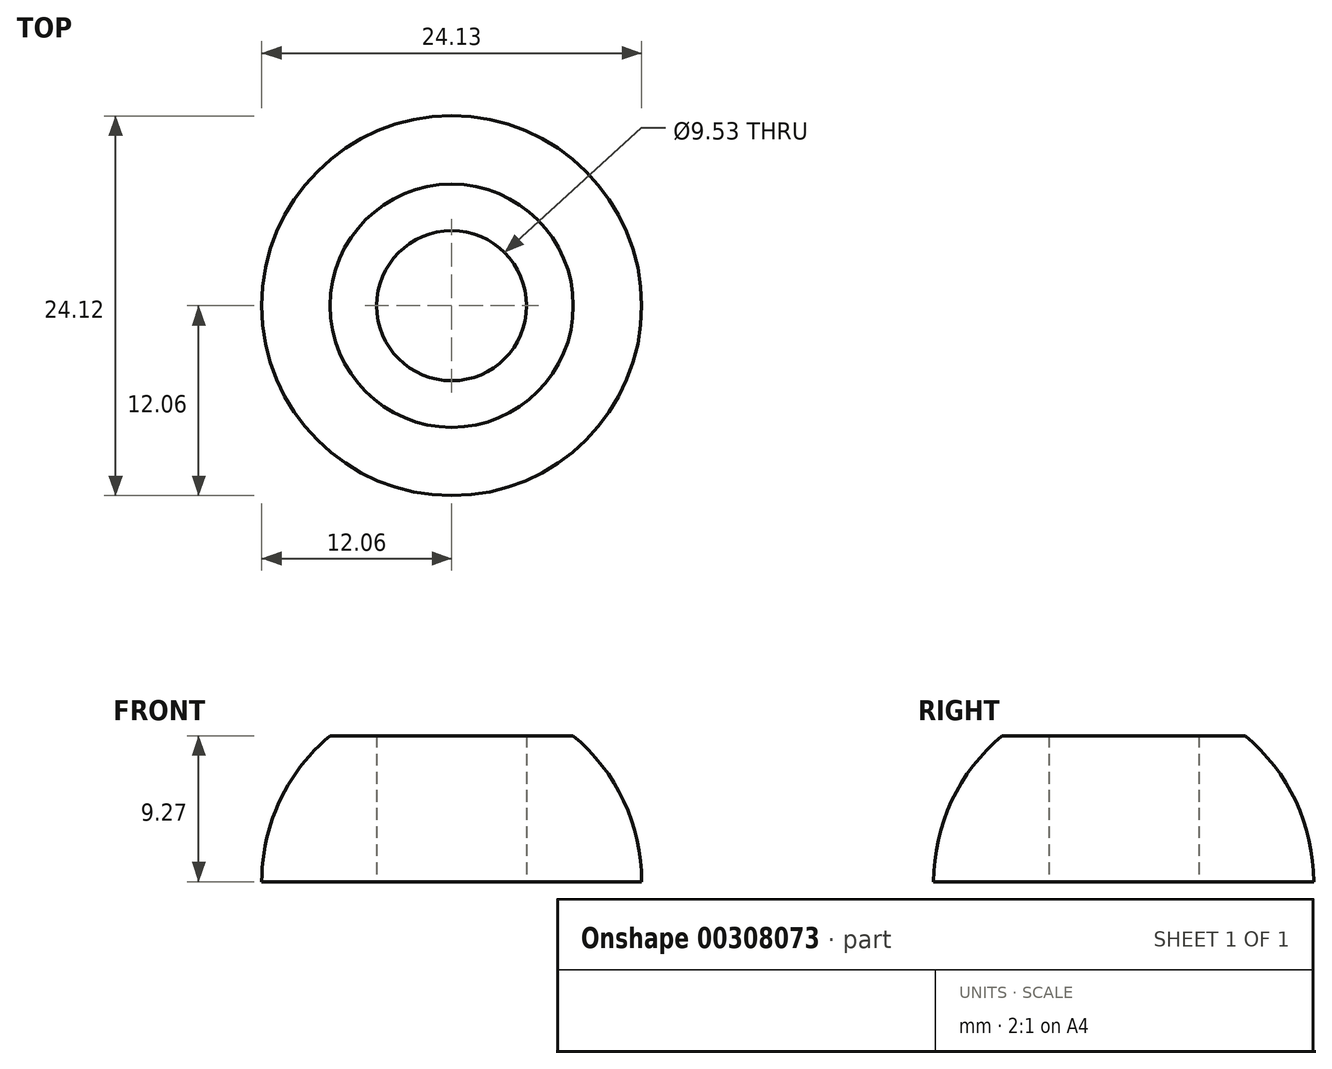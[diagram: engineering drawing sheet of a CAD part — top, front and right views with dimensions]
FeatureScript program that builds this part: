
annotation { "Feature Type Name" : "Feature", "Feature Type Description" : "" }
export const myFeature = defineFeature(function(context is Context, id is Id, definition is map)
    precondition{}
    {
        {
            var Q0;
            Q0=qCreatedBy(makeId("Front.planeOp"),FACE);
            var sketch = newSketch(context, id + "F0", { "sketchPlane" : qUnion([Q0])});
            skArc(sketch, "E0", {"start": v(12.07, 0) * mm, "mid": v(10.93, 5.12) * mm, "end": v(7.72, 9.27) * mm});
            skLineSegment(sketch, "E1", {"start": v(4.76, 0) * mm, "end": v(12.07, 0) * mm});
            skLineSegment(sketch, "E2.0", {"start": v(4.76, 9.27) * mm, "end": v(7.72, 9.27) * mm});
            skLineSegment(sketch, "E3.trimOffspring", {"start": v(4.76, 9.27) * mm, "end": v(4.76, 0) * mm});
            skLineSegment(sketch, "E4", {"start": v(0, 0) * mm, "end": v(0, 9.27) * mm});
            skSolve(sketch);
        }
        {
            var Q0;
            Q0 = qSketchRegion(id + "F0", true);
            var Q1;
            Q1=sQuery(id+"F0.wireOp",EDGE,"E4");
            revolve(context, id + "F1", {"surfaceOperationType" : NewSurfaceOperationType.NEW, "entities" : qUnion([Q0]), "axis" : qUnion([Q1]), "revolveType" : RevolveType.FULL});
        }
    });
